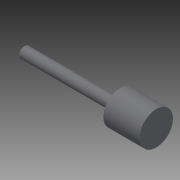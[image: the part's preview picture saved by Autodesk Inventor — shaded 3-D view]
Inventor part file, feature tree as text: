
AUTODESK INVENTOR PART (.ipt)
format: ipt  version: 2014 (Build 180170000, 170)  size: 118,272 bytes
history: native  units: in
note: dims shown in document units (in); Inventor stores cm internally (conversion verified against a paired STEP export)
features: other x49, revolve x2, sketch x2
ambient origin geometry x8: Origin, YZ Plane, XZ Plane, XY Plane, X Axis, Y Axis, Z Axis, Center Point
bodies: Solid1 (feature_tree)
feature tree (53):
  revolve  "Revolution1"  Angle=360.0deg
  revolve  "Revolution2"  [1 undecoded]
  other  "h1_XY"
  other  "h1_YZ"
  other  "h1_ZX"
  other  "h1_X"
  other  "h1_Y"
  other  "h1_Z"
  other  "h1_Center"
  other  "h2_XY"
  other  "h2_YZ"
  other  "h2_ZX"
  other  "h2_X"
  other  "h2_Y"
  other  "h2_Z"
  other  "h2_Center"
  other  "k1_XY"
  other  "k1_YZ"
  other  "k1_ZX"
  other  "k1_X"
  other  "k1_Y"
  other  "k1_Z"
  other  "k1_Center"
  other  "k2_XY"
  other  "k2_YZ"
  other  "k2_ZX"
  other  "k2_X"
  other  "k2_Y"
  other  "k2_Z"
  other  "k2_Center"
  other  "start_XY"
  other  "start_YZ"
  other  "start_ZX"
  other  "start_X"
  other  "start_Y"
  other  "start_Z"
  other  "start_Center"
  other  "to_prc_XY"
  other  "to_prc_YZ"
  other  "to_prc_ZX"
  other  "to_prc_X"
  other  "to_prc_Y"
  other  "to_prc_Z"
  other  "to_prc_Center"
  other  "to_rod_guide_XY"
  other  "to_rod_guide_YZ"
  other  "to_rod_guide_ZX"
  other  "to_rod_guide_X"
  other  "to_rod_guide_Y"
  other  "to_rod_guide_Z"
  other  "to_rod_guide_Center"
  sketch  "Sketch_5"  dims[d0=360.0deg d1=360.0deg]
  sketch  "Sketch_14"
note: 1 required parameter value undecoded (feature->parameter linkage not recoverable at this tier; creation-order binding heuristic only, values carry confidence <= 0.55)
